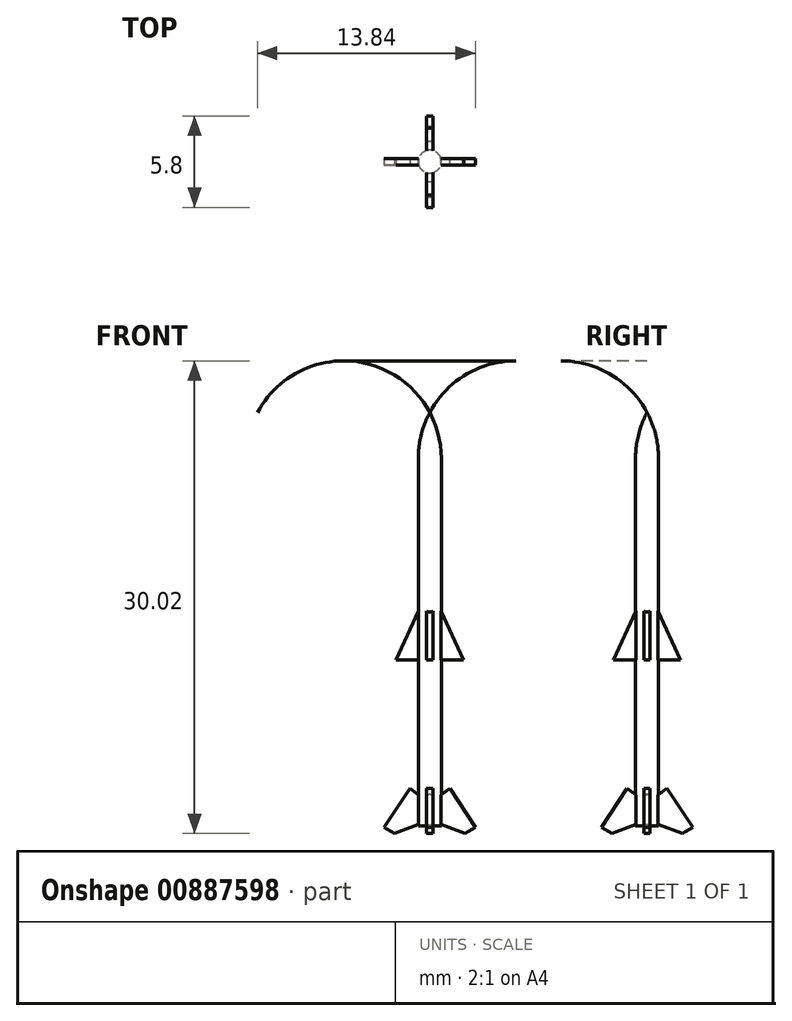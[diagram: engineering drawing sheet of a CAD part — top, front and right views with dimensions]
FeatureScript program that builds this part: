
annotation { "Feature Type Name" : "Feature", "Feature Type Description" : "" }
export const myFeature = defineFeature(function(context is Context, id is Id, definition is map)
    precondition{}
    {
        {
            var Q0;
            Q0=qCreatedBy(makeId("Front.planeOp"),FACE);
            var sketch = newSketch(context, id + "F0", { "sketchPlane" : qUnion([Q0])});
            skLineSegment(sketch, "E0", {"start": v(0, 0) * mm, "end": v(0, 26.25) * mm});
            skLineSegment(sketch, "E1", {"start": v(0.73, 23.33) * mm, "end": v(0.73, 0) * mm});
            skLineSegment(sketch, "E2", {"start": v(0.73, 0) * mm, "end": v(0, 0) * mm});
            skArc(sketch, "E3", {"start": v(0.73, 23.33) * mm, "mid": v(0.54, 24.84) * mm, "end": v(0, 26.25) * mm});
            skSolve(sketch);
        }
        {
            var Q0;
            {var subQ0=sQuery(id+"F0.wireOp",EDGE,"mrwio9nY-PsAZ-Zbfy-NhIU-sYq0QVbgGXAG");Q0=makeQuery(id+"F0.imprint","IMPRINT",FACE,{"disambiguationData":[TD([[makeQuery(id+"F0.imprint","IMPRINT",EDGE,{"derivedFrom":subQ0}),-1.0]])]});}
            var Q1;
            Q1=makeQuery(id+"F0.imprint","IMPRINT",FACE,{"disambiguationData":[TD([[makeQuery(id+"F0.imprint","IMPRINT",EDGE,{"derivedFrom":sQuery(id+"F0.wireOp",EDGE,"rEedh4zr-IGRr-Hqzj-sDLB-QnI7VE1V64O6.bottom")}),-1.0]])]});
            var Q2;
            Q2=makeQuery(id+"F0.imprint","IMPRINT",FACE,{"disambiguationData":[TD([[makeQuery(id+"F0.imprint","IMPRINT",EDGE,{"derivedFrom":sQuery(id+"F0.wireOp",EDGE,"E0")}),-1.0]])]});
            var Q3;
            Q3=makeQuery(id+"F0.imprint","IMPRINT",FACE,{"disambiguationData":[TD([[makeQuery(id+"F0.imprint","IMPRINT",EDGE,{"derivedFrom":sQuery(id+"F0.wireOp",EDGE,"p5wuz8j9-3HT4-kWwn-DjtP-lJmqTNSXSBJY.bottom")}),-1.0]])]});
            var Q4;
            Q4=sQuery(id+"F0.wireOp",EDGE,"E0");
            revolve(context, id + "F1", {"surfaceOperationType" : NewSurfaceOperationType.NEW, "entities" : qUnion([Q0, Q1, Q2, Q3]), "axis" : qUnion([Q4]), "revolveType" : RevolveType.FULL});
        }
        {
            var Q0;
            Q0=qCreatedBy(makeId("Front.planeOp"),FACE);
            var sketch = newSketch(context, id + "F2", { "sketchPlane" : qUnion([Q0])});
            skLineSegment(sketch, "E4", {"start": v(0, 0) * mm, "end": v(0, 16.56) * mm});
            skLineSegment(sketch, "E5", {"start": v(0.73, -0.2) * mm, "end": v(0.73, 32.87) * mm, "construction": true});
            skLineSegment(sketch, "E6.0", {"start": v(0.73, 0) * mm, "end": v(-0.73, 0) * mm});
            skLineSegment(sketch, "E7", {"start": v(0.73, -0.2) * mm, "end": v(0.73, 0) * mm});
            skLineSegment(sketch, "E8", {"start": v(0, 10.52) * mm, "end": v(2.14, 10.52) * mm});
            skLineSegment(sketch, "E9", {"start": v(2.14, 10.52) * mm, "end": v(0, 15.16) * mm});
            skPoint(sketch, "E10", {"position": v(0.73, 13.58) * mm});
            skLineSegment(sketch, "E11", {"start": v(0, 0.34) * mm, "end": v(2.24, -0.49) * mm});
            skLineSegment(sketch, "E12", {"start": v(2.24, -0.49) * mm, "end": v(2.9, -0.1) * mm});
            skLineSegment(sketch, "E13", {"start": v(2.9, -0.1) * mm, "end": v(1.27, 2.36) * mm});
            skLineSegment(sketch, "E14", {"start": v(1.27, 2.36) * mm, "end": v(0, 1.47) * mm});
            skPoint(sketch, "E15", {"position": v(0.73, 1.98) * mm});
            skPoint(sketch, "E16", {"position": v(0.73, 0.07) * mm});
            skSolve(sketch);
        }
        {
            var Q0;
            Q0=qSketchRegion(id+"F2",true);
            extrude(context, id + "F3", {"entities" : qUnion([Q0]), "operationType" : NewBodyOperationType.ADD, "depth" : .4 * mm, "offsetDistance" : 25 * mm, "symmetric" : true});
        }
        {
            var Q0;
            Q0=makeQuery(id+"F1.opRevolve","SWEPT_BODY",BODY,{"disambiguationData":[OSD([sQuery(id+"F0.wireOp",EDGE,"E0"),sQuery(id+"F0.wireOp",EDGE,"E1"),sQuery(id+"F0.wireOp",EDGE,"E2"),sQuery(id+"F0.wireOp",EDGE,"2EiOItwe-9FNA-eY8p-DkXH-AMy5AHyUmzZA"),sQuery(id+"F0.wireOp",EDGE,"lF35QjYl-MEgV-fRWE-0Yr6-Bt5vS8A7brRf")])]});
            var Q1;
            Q1=makeQuery(id+"F1.opRevolve","SWEPT_FACE",FACE,{"disambiguationData":[OSD([sQuery(id+"F0.wireOp",EDGE,"E1")])]});
            circularPattern(context, id + "F4", {"operationType" : NewBodyOperationType.ADD, "entities" : qUnion([Q0]), "axis" : qUnion([Q1]), "angle" : 360 * degree, "instanceCount" : 4, "equalSpace" : true, "computeTransformsWithoutBuiltin" : true});
        }
    });
